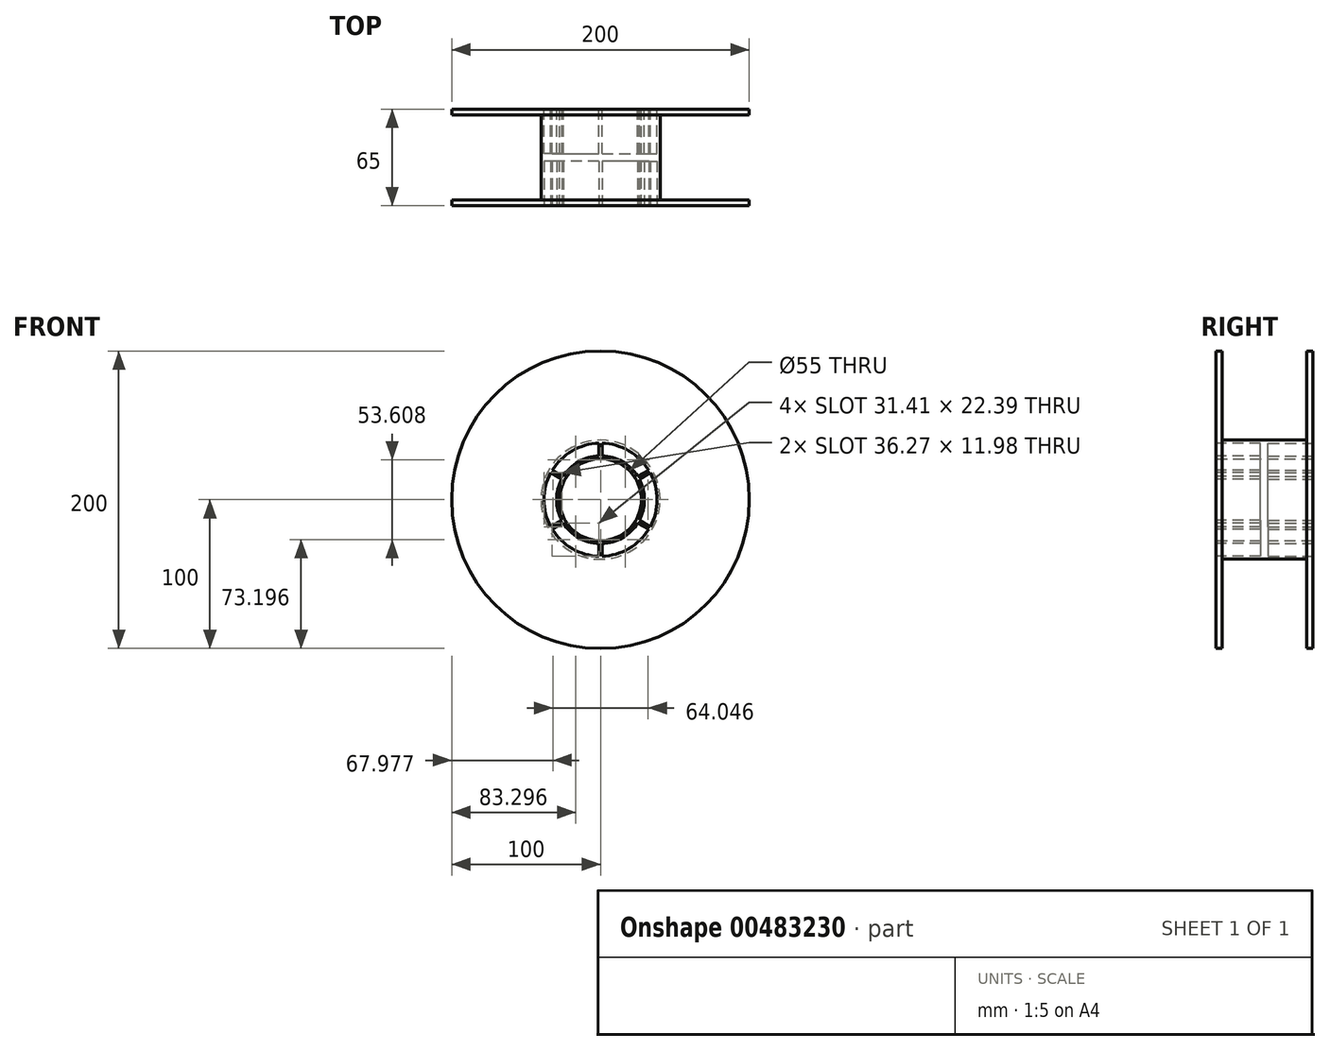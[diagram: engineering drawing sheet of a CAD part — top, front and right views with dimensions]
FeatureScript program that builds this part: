
annotation { "Feature Type Name" : "Feature", "Feature Type Description" : "" }
export const myFeature = defineFeature(function(context is Context, id is Id, definition is map)
    precondition{}
    {
        {
            var Q0;
            Q0=qCreatedBy(makeId("Front.planeOp"),FACE);
            var sketch = newSketch(context, id + "F0", { "sketchPlane" : qUnion([Q0])});
            skCircle(sketch, "E0", {"center": v(0, 0) * mm, "radius": 27.5 * mm});
            skCircle(sketch, "E1", {"center": v(0, 0) * mm, "radius": 100 * mm});
            skSolve(sketch);
        }
        {
            var Q0;
            Q0 = qSketchRegion(id + "F0", true);
            extrude(context, id + "F1", {"entities" : qUnion([Q0]), "depth" : 4 * mm});
        }
        {
            var Q0;
            Q0=makeQuery(id+"F1.opExtrude","CAP_FACE",FACE,{"disambiguationData":[OSD([sQuery(id+"F0.wireOp",EDGE,"E0"),sQuery(id+"F0.wireOp",EDGE,"E1")])],"isStart":false});
            var sketch = newSketch(context, id + "F2", { "sketchPlane" : qUnion([Q0])});
            skCircle(sketch, "E2", {"center": v(0, 0) * mm, "radius": 27.5 * mm});
            skCircle(sketch, "E3", {"center": v(0, 0) * mm, "radius": 40 * mm});
            skSolve(sketch);
        }
        {
            var Q0;
            Q0 = qSketchRegion(id + "F2", true);
            extrude(context, id + "F3", {"entities" : qUnion([Q0]), "operationType" : NewBodyOperationType.ADD, "depth" : 57 * mm});
        }
        {
            var Q0;
            Q0=makeQuery(id+"F3.opExtrude","CAP_FACE",FACE,{"disambiguationData":[OSD([sQuery(id+"F2.wireOp",EDGE,"E2"),sQuery(id+"F2.wireOp",EDGE,"E3")])],"isStart":false});
            var sketch = newSketch(context, id + "F4", { "sketchPlane" : qUnion([Q0])});
            skCircle(sketch, "E4", {"center": v(0, 0) * mm, "radius": 27.5 * mm});
            skCircle(sketch, "E5", {"center": v(0, 0) * mm, "radius": 100 * mm});
            skSolve(sketch);
        }
        {
            var Q0;
            Q0 = qSketchRegion(id + "F4", true);
            extrude(context, id + "F5", {"entities" : qUnion([Q0]), "operationType" : NewBodyOperationType.ADD, "depth" : 4 * mm});
        }
        {
            var Q0;
            Q0=makeQuery(id+"F5.opExtrude","CAP_FACE",FACE,{"disambiguationData":[OSD([sQuery(id+"F4.wireOp",EDGE,"E4"),sQuery(id+"F4.wireOp",EDGE,"E5")])],"isStart":false});
            var sketch = newSketch(context, id + "F6", { "sketchPlane" : qUnion([Q0])});
            skArc(sketch, "E6", {"start": v(1, 38) * mm, "mid": v(19, 32.92) * mm, "end": v(32.4, 19.87) * mm});
            skArc(sketch, "E7", {"start": v(1, 29.48) * mm, "mid": v(14.75, 25.55) * mm, "end": v(25.03, 15.6) * mm});
            skLineSegment(sketch, "E8.trimOffspring", {"start": v(1, 29.48) * mm, "end": v(1, 38) * mm});
            skLineSegment(sketch, "E9.trimOffspring", {"start": v(25.03, 15.6) * mm, "end": v(32.4, 19.87) * mm});
            skLineSegment(sketch, "E10.1.0", {"start": v(-1, 29.48) * mm, "end": v(-1, 38) * mm});
            skLineSegment(sketch, "E10.1.1", {"start": v(-25.03, 15.6) * mm, "end": v(-32.4, 19.87) * mm});
            skArc(sketch, "E10.1.2", {"start": v(-25.03, 15.6) * mm, "mid": v(-14.75, 25.55) * mm, "end": v(-1, 29.48) * mm});
            skArc(sketch, "E10.1.3", {"start": v(-32.4, 19.87) * mm, "mid": v(-19, 32.92) * mm, "end": v(-1, 38) * mm});
            skLineSegment(sketch, "E10.2.0", {"start": v(-26.03, 13.88) * mm, "end": v(-33.4, 18.13) * mm});
            skLineSegment(sketch, "E10.2.1", {"start": v(-26.03, -13.88) * mm, "end": v(-33.4, -18.13) * mm});
            skArc(sketch, "E10.2.2", {"start": v(-26.03, -13.88) * mm, "mid": v(-29.5, 0) * mm, "end": v(-26.03, 13.88) * mm});
            skArc(sketch, "E10.2.3", {"start": v(-33.4, -18.13) * mm, "mid": v(-38.01, 0) * mm, "end": v(-33.4, 18.13) * mm});
            skLineSegment(sketch, "E10.3.0", {"start": v(-25.03, -15.6) * mm, "end": v(-32.4, -19.87) * mm});
            skLineSegment(sketch, "E10.3.1", {"start": v(-1, -29.48) * mm, "end": v(-1, -38) * mm});
            skArc(sketch, "E10.3.2", {"start": v(-1, -29.48) * mm, "mid": v(-14.75, -25.55) * mm, "end": v(-25.03, -15.6) * mm});
            skArc(sketch, "E10.3.3", {"start": v(-1, -38) * mm, "mid": v(-19, -32.92) * mm, "end": v(-32.4, -19.87) * mm});
            skLineSegment(sketch, "E10.4.0", {"start": v(1, -29.48) * mm, "end": v(1, -38) * mm});
            skLineSegment(sketch, "E10.4.1", {"start": v(25.03, -15.6) * mm, "end": v(32.4, -19.87) * mm});
            skArc(sketch, "E10.4.2", {"start": v(25.03, -15.6) * mm, "mid": v(14.75, -25.55) * mm, "end": v(1, -29.48) * mm});
            skArc(sketch, "E10.4.3", {"start": v(32.4, -19.87) * mm, "mid": v(19, -32.92) * mm, "end": v(1, -38) * mm});
            skLineSegment(sketch, "E10.5.0", {"start": v(26.03, -13.88) * mm, "end": v(33.4, -18.13) * mm});
            skLineSegment(sketch, "E10.5.1", {"start": v(26.03, 13.88) * mm, "end": v(33.4, 18.13) * mm});
            skArc(sketch, "E10.5.2", {"start": v(26.03, 13.88) * mm, "mid": v(29.5, 0) * mm, "end": v(26.03, -13.88) * mm});
            skArc(sketch, "E10.5.3", {"start": v(33.4, 18.13) * mm, "mid": v(38.01, 0) * mm, "end": v(33.4, -18.13) * mm});
            skSolve(sketch);
        }
        {
            var Q0;
            Q0 = qSketchRegion(id + "F6", true);
            extrude(context, id + "F7", {"entities" : qUnion([Q0]), "operationType" : NewBodyOperationType.REMOVE, "oppositeDirection" : true, "depth" : 30 * mm});
        }
        {
            var Q0;
            Q0=makeQuery(id+"F1.opExtrude","CAP_FACE",FACE,{"disambiguationData":[OSD([sQuery(id+"F0.wireOp",EDGE,"E0"),sQuery(id+"F0.wireOp",EDGE,"E1")])],"isStart":true});
            var sketch = newSketch(context, id + "F8", { "sketchPlane" : qUnion([Q0])});
            skArc(sketch, "E11", {"start": v(1, 38) * mm, "mid": v(19, 32.92) * mm, "end": v(32.4, 19.87) * mm});
            skArc(sketch, "E12", {"start": v(1, 29.48) * mm, "mid": v(14.75, 25.55) * mm, "end": v(25.03, 15.6) * mm});
            skLineSegment(sketch, "E13.trimOffspring", {"start": v(1, 29.48) * mm, "end": v(1, 38) * mm});
            skLineSegment(sketch, "E14.trimOffspring", {"start": v(25.03, 15.6) * mm, "end": v(32.4, 19.87) * mm});
            skLineSegment(sketch, "E15.1.0", {"start": v(-25.03, 15.6) * mm, "end": v(-32.4, 19.87) * mm});
            skArc(sketch, "E15.1.1", {"start": v(-25.03, 15.6) * mm, "mid": v(-14.75, 25.55) * mm, "end": v(-1, 29.48) * mm});
            skLineSegment(sketch, "E15.1.2", {"start": v(-1, 29.48) * mm, "end": v(-1, 38) * mm});
            skArc(sketch, "E15.1.3", {"start": v(-32.4, 19.87) * mm, "mid": v(-19, 32.92) * mm, "end": v(-1, 38) * mm});
            skLineSegment(sketch, "E15.2.0", {"start": v(-26.03, -13.88) * mm, "end": v(-33.4, -18.13) * mm});
            skArc(sketch, "E15.2.1", {"start": v(-26.03, -13.88) * mm, "mid": v(-29.5, 0) * mm, "end": v(-26.03, 13.88) * mm});
            skLineSegment(sketch, "E15.2.2", {"start": v(-26.03, 13.88) * mm, "end": v(-33.4, 18.13) * mm});
            skArc(sketch, "E15.2.3", {"start": v(-33.4, -18.13) * mm, "mid": v(-38.01, 0) * mm, "end": v(-33.4, 18.13) * mm});
            skLineSegment(sketch, "E15.3.0", {"start": v(-1, -29.48) * mm, "end": v(-1, -38) * mm});
            skArc(sketch, "E15.3.1", {"start": v(-1, -29.48) * mm, "mid": v(-14.75, -25.55) * mm, "end": v(-25.03, -15.6) * mm});
            skLineSegment(sketch, "E15.3.2", {"start": v(-25.03, -15.6) * mm, "end": v(-32.4, -19.87) * mm});
            skArc(sketch, "E15.3.3", {"start": v(-1, -38) * mm, "mid": v(-19, -32.92) * mm, "end": v(-32.4, -19.87) * mm});
            skLineSegment(sketch, "E15.4.0", {"start": v(25.03, -15.6) * mm, "end": v(32.4, -19.87) * mm});
            skArc(sketch, "E15.4.1", {"start": v(25.03, -15.6) * mm, "mid": v(14.75, -25.55) * mm, "end": v(1, -29.48) * mm});
            skLineSegment(sketch, "E15.4.2", {"start": v(1, -29.48) * mm, "end": v(1, -38) * mm});
            skArc(sketch, "E15.4.3", {"start": v(32.4, -19.87) * mm, "mid": v(19, -32.92) * mm, "end": v(1, -38) * mm});
            skLineSegment(sketch, "E15.5.0", {"start": v(26.03, 13.88) * mm, "end": v(33.4, 18.13) * mm});
            skArc(sketch, "E15.5.1", {"start": v(26.03, 13.88) * mm, "mid": v(29.5, 0) * mm, "end": v(26.03, -13.88) * mm});
            skLineSegment(sketch, "E15.5.2", {"start": v(26.03, -13.88) * mm, "end": v(33.4, -18.13) * mm});
            skArc(sketch, "E15.5.3", {"start": v(33.4, 18.13) * mm, "mid": v(38.01, 0) * mm, "end": v(33.4, -18.13) * mm});
            skSolve(sketch);
        }
        {
            var Q0;
            Q0 = qSketchRegion(id + "F8", true);
            extrude(context, id + "F9", {"entities" : qUnion([Q0]), "operationType" : NewBodyOperationType.REMOVE, "oppositeDirection" : true, "depth" : 30 * mm});
        }
    });
